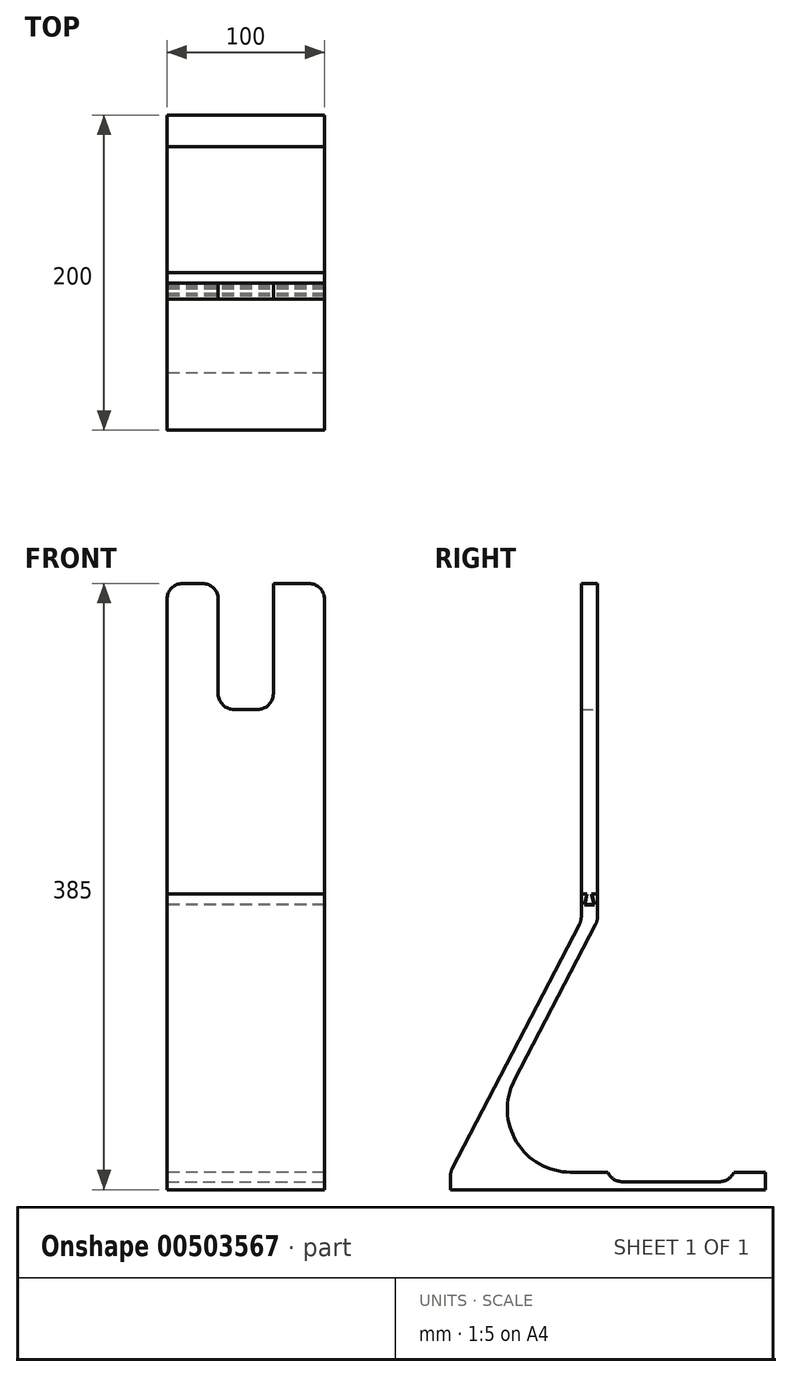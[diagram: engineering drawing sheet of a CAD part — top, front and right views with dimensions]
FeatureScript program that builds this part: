
annotation { "Feature Type Name" : "Feature", "Feature Type Description" : "" }
export const myFeature = defineFeature(function(context is Context, id is Id, definition is map)
    precondition{}
    {
        {
            var Q0;
            Q0=qCreatedBy(makeId("Right.planeOp"),FACE);
            var sketch = newSketch(context, id + "F0", { "sketchPlane" : qUnion([Q0])});
            skLineSegment(sketch, "E0.bottom", {"start": v(136.52, -18.48) * mm, "end": v(116.52, -18.48) * mm});
            skLineSegment(sketch, "E0.top", {"start": v(136.52, -29.6) * mm, "end": v(-63.48, -29.6) * mm});
            skLineSegment(sketch, "E0.left", {"start": v(136.52, -18.48) * mm, "end": v(136.52, -29.6) * mm});
            skLineSegment(sketch, "E0.right", {"start": v(-63.48, -18.48) * mm, "end": v(-63.48, -29.6) * mm});
            skLineSegment(sketch, "E1.bottom", {"start": v(19.6, 355.4) * mm, "end": v(29.89, 355.4) * mm});
            skLineSegment(sketch, "E1.top", {"start": v(19.6, 141.2) * mm, "end": v(29.89, 141.2) * mm});
            skLineSegment(sketch, "E1.left", {"start": v(19.6, 355.4) * mm, "end": v(19.6, 141.2) * mm});
            skLineSegment(sketch, "E1.right", {"start": v(29.89, 355.4) * mm, "end": v(29.89, 141.2) * mm});
            skLineSegment(sketch, "E2", {"start": v(19.6, 141.2) * mm, "end": v(-63.48, -18.48) * mm});
            skLineSegment(sketch, "E3", {"start": v(29.89, 141.2) * mm, "end": v(-53.2, -18.48) * mm});
            skLineSegment(sketch, "E4.top", {"start": v(36.52, -24.6) * mm, "end": v(116.52, -24.6) * mm});
            skLineSegment(sketch, "E4.left", {"start": v(36.52, -18.48) * mm, "end": v(36.52, -24.6) * mm});
            skLineSegment(sketch, "E4.right", {"start": v(116.52, -18.48) * mm, "end": v(116.52, -24.6) * mm});
            skLineSegment(sketch, "E5.trimOffspring", {"start": v(36.52, -18.48) * mm, "end": v(-63.48, -18.48) * mm});
            skLineSegment(sketch, "E6", {"start": v(19.6, 158.25) * mm, "end": v(23.1, 158.25) * mm});
            skLineSegment(sketch, "E7", {"start": v(23.1, 158.25) * mm, "end": v(21.6, 151.23) * mm});
            skLineSegment(sketch, "E8", {"start": v(21.6, 151.23) * mm, "end": v(27.89, 151.23) * mm});
            skLineSegment(sketch, "E9", {"start": v(27.89, 151.23) * mm, "end": v(26.39, 158.25) * mm});
            skLineSegment(sketch, "E10", {"start": v(26.39, 158.25) * mm, "end": v(29.89, 158.25) * mm});
            skSolve(sketch);
        }
        {
            var Q0;
            Q0=makeQuery(id+"F0.imprint","IMPRINT",FACE,{"disambiguationData":[TD([[makeQuery(id+"F0.imprint","IMPRINT",EDGE,{"derivedFrom":sQuery(id+"F0.wireOp",EDGE,"E0.bottom")}),1.0]])]});
            var Q1;
            {var subQ1=sQuery(id+"F0.wireOp",EDGE,"E1.top");Q1=makeQuery(id+"F0.imprint","IMPRINT",FACE,{"disambiguationData":[TD([[makeQuery(id+"F0.imprint","IMPRINT",EDGE,{"derivedFrom":subQ1}),1.0]])]});}
            var Q2;
            Q2=makeQuery(id+"F0.imprint","IMPRINT",FACE,{"disambiguationData":[TD([[makeQuery(id+"F0.imprint","IMPRINT",EDGE,{"derivedFrom":sQuery(id+"F0.wireOp",EDGE,"E1.top")}),-1.0]])]});
            extrude(context, id + "F1", {"entities" : qUnion([Q0, Q1, Q2]), "depth" : 100 * mm});
        }
        {
            var Q0;
            Q0=makeQuery(id+"F1.opExtrude","SWEPT_EDGE",EDGE,{"disambiguationData":[OSD([sQuery(id+"F0.wireOp",EDGE,"E4.top"),sQuery(id+"F0.wireOp",EDGE,"E4.right")])]});
            var Q1;
            Q1=makeQuery(id+"F1.opExtrude","SWEPT_EDGE",EDGE,{"disambiguationData":[OSD([sQuery(id+"F0.wireOp",EDGE,"E4.top"),sQuery(id+"F0.wireOp",EDGE,"E4.left")])]});
            var Q2;
            Q2=makeQuery(id+"F1.opExtrude","SWEPT_EDGE",EDGE,{"disambiguationData":[OSD([sQuery(id+"F0.wireOp",EDGE,"E1.top"),sQuery(id+"F0.wireOp",EDGE,"E1.right"),sQuery(id+"F0.wireOp",EDGE,"E3")])]});
            var Q3;
            Q3=makeQuery(id+"F1.opExtrude","SWEPT_EDGE",EDGE,{"disambiguationData":[OSD([sQuery(id+"F0.wireOp",EDGE,"E1.top"),sQuery(id+"F0.wireOp",EDGE,"E1.left"),sQuery(id+"F0.wireOp",EDGE,"E2")])]});
            var Q4;
            Q4=makeQuery(id+"F1.opExtrude","SWEPT_EDGE",EDGE,{"disambiguationData":[OSD([sQuery(id+"F0.wireOp",EDGE,"E0.right"),sQuery(id+"F0.wireOp",EDGE,"E2"),sQuery(id+"F0.wireOp",EDGE,"E5.trimOffspring")])]});
            fillet(context, id + "F2", {"entities" : qUnion([Q0, Q1, Q2, Q3, Q4]), "radius" : 10 * mm, "tangentPropagation" : true, "allowEdgeOverflow" : false});
        }
        {
            var Q0;
            {var subQ2=sQuery(id+"F0.wireOp",EDGE,"E1.bottom");Q0=makeQuery(id+"F0.imprint","IMPRINT",FACE,{"disambiguationData":[TD([[makeQuery(id+"F0.imprint","IMPRINT",EDGE,{"derivedFrom":subQ2}),-1.0]])]});}
            var sketch = newSketch(context, id + "F3", { "sketchPlane" : qUnion([Q0])});
            skLineSegment(sketch, "E11.bottom", {"start": v(19.6, 355.4) * mm, "end": v(29.89, 355.4) * mm});
            skLineSegment(sketch, "E11.left", {"start": v(19.6, 355.4) * mm, "end": v(19.6, 158.25) * mm});
            skLineSegment(sketch, "E11.right", {"start": v(29.89, 355.4) * mm, "end": v(29.89, 158.25) * mm});
            skLineSegment(sketch, "E12", {"start": v(19.6, 158.25) * mm, "end": v(23.1, 158.25) * mm});
            skLineSegment(sketch, "E13", {"start": v(26.39, 158.25) * mm, "end": v(29.89, 158.25) * mm});
            skLineSegment(sketch, "E14", {"start": v(23.1, 158.25) * mm, "end": v(23.3, 158.25) * mm});
            skLineSegment(sketch, "E15", {"start": v(26.39, 158.25) * mm, "end": v(26.19, 158.25) * mm});
            skLineSegment(sketch, "E16", {"start": v(27.66, 151.43) * mm, "end": v(26.19, 158.25) * mm});
            skLineSegment(sketch, "E17", {"start": v(21.83, 151.43) * mm, "end": v(23.3, 158.25) * mm});
            skLineSegment(sketch, "E18", {"start": v(24.56, 151.43) * mm, "end": v(21.83, 151.43) * mm});
            skLineSegment(sketch, "E19", {"start": v(21.83, 151.43) * mm, "end": v(27.66, 151.43) * mm});
            skSolve(sketch);
        }
        {
            var Q0;
            Q0=makeQuery(id+"F3.imprint","IMPRINT",FACE,{"disambiguationData":[TD([[makeQuery(id+"F3.imprint","IMPRINT",EDGE,{"derivedFrom":sQuery(id+"F3.wireOp",EDGE,"E11.bottom")}),-1.0]])]});
            extrude(context, id + "F4", {"entities" : qUnion([Q0]), "depth" : 100 * mm});
        }
        {
            var Q0;
            Q0=makeQuery(id+"F4.opExtrude","SWEPT_FACE",FACE,{"disambiguationData":[OSD([sQuery(id+"F3.wireOp",EDGE,"E11.right")])]});
            var sketch = newSketch(context, id + "F5", { "sketchPlane" : qUnion([Q0])});
            skLineSegment(sketch, "E20.bottom", {"start": v(-67.5, 355.4) * mm, "end": v(-32.5, 355.4) * mm});
            skLineSegment(sketch, "E20.top", {"start": v(-67.5, 275.4) * mm, "end": v(-32.5, 275.4) * mm});
            skLineSegment(sketch, "E20.left", {"start": v(-67.5, 355.4) * mm, "end": v(-67.5, 275.4) * mm});
            skLineSegment(sketch, "E20.right", {"start": v(-32.5, 355.4) * mm, "end": v(-32.5, 275.4) * mm});
            skSolve(sketch);
        }
        {
            var Q0;
            Q0 = qSketchRegion(id + "F5", true);
            extrude(context, id + "F6", {"entities" : qUnion([Q0]), "operationType" : NewBodyOperationType.REMOVE, "oppositeDirection" : true, "depth" : 25 * mm});
        }
        {
            var Q0;
            Q0=makeQuery(id+"F6.boolean.opBoolean","COPY",EDGE,{"derivedFrom":makeQuery(id+"F6.opExtrude","SWEPT_EDGE",EDGE,{"disambiguationData":[OSD([sQuery(id+"F5.wireOp",EDGE,"E20.top"),sQuery(id+"F5.wireOp",EDGE,"E20.right")])]})});
            var Q1;
            Q1=makeQuery(id+"F6.boolean.opBoolean","COPY",EDGE,{"derivedFrom":makeQuery(id+"F6.opExtrude","SWEPT_EDGE",EDGE,{"disambiguationData":[OSD([sQuery(id+"F5.wireOp",EDGE,"E20.top"),sQuery(id+"F5.wireOp",EDGE,"E20.left")])]})});
            var Q2;
            Q2=makeQuery(id+"F6.boolean.opBoolean","COPY",EDGE,{"derivedFrom":makeQuery(id+"F6.opExtrude","SWEPT_EDGE",EDGE,{"disambiguationData":[OSD([sQuery(id+"F3.wireOp",EDGE,"E11.bottom"),sQuery(id+"F3.wireOp",EDGE,"E11.right"),sQuery(id+"F5.wireOp",EDGE,"E20.bottom"),sQuery(id+"F5.wireOp",EDGE,"E20.right")])]})});
            var Q3;
            Q3=makeQuery(id+"F6.boolean.opBoolean","COPY",EDGE,{"derivedFrom":makeQuery(id+"F6.opExtrude","SWEPT_EDGE",EDGE,{"disambiguationData":[OSD([sQuery(id+"F3.wireOp",EDGE,"E11.bottom"),sQuery(id+"F3.wireOp",EDGE,"E11.right"),sQuery(id+"F5.wireOp",EDGE,"E20.bottom"),sQuery(id+"F5.wireOp",EDGE,"E20.left")])]})});
            var Q4;
            Q4=makeQuery(id+"F4.opExtrude","CAP_EDGE",EDGE,{"disambiguationData":[OSD([sQuery(id+"F3.wireOp",EDGE,"E11.bottom")])],"isStart":false});
            var Q5;
            Q5=makeQuery(id+"F4.opExtrude","CAP_EDGE",EDGE,{"disambiguationData":[OSD([sQuery(id+"F3.wireOp",EDGE,"E11.bottom")])],"isStart":true});
            fillet(context, id + "F7", {"entities" : qUnion([Q0, Q1, Q2, Q3, Q4, Q5]), "radius" : 10 * mm, "tangentPropagation" : true, "allowEdgeOverflow" : false});
        }
        {
            var Q0;
            Q0=makeQuery(id+"F1.opExtrude","SWEPT_EDGE",EDGE,{"disambiguationData":[OSD([sQuery(id+"F0.wireOp",EDGE,"E3"),sQuery(id+"F0.wireOp",EDGE,"E5.trimOffspring")])]});
            fillet(context, id + "F8", {"entities" : qUnion([Q0]), "radius" : 40 * mm, "tangentPropagation" : true, "allowEdgeOverflow" : false});
        }
    });
